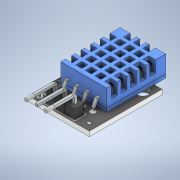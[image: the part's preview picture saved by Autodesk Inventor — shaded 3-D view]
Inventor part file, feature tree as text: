
AUTODESK INVENTOR PART (.ipt)
format: ipt  version: 2021 (Build 250183000, 183)  size: 781,824 bytes
history: native  units: mm
features: projected_geometry x5, boolean_combine x1, extrude x1, sketch x1
ambient origin geometry x8: Origin, YZ Plane, XZ Plane, XY Plane, X Axis, Y Axis, Z Axis, Center Point
bodies: Solid1 (feature_tree), Solid2 (feature_tree), Solid3 (feature_tree), Solid4 (feature_tree), Solid5 (feature_tree), Solid6 (feature_tree), Solid7 (feature_tree), Solid8 (feature_tree), Body1 (feature_tree), Body2 (feature_tree), Body3 (feature_tree), Body4 (feature_tree), Body5 (feature_tree), Body6 (feature_tree), Body7 (feature_tree), Body8 (feature_tree)
feature tree (8):
  boolean_combine  "Combine1"
  extrude  "Extrusion1"  [1 undecoded]
  sketch  "Sketch1"  dims[d0=2.0mm d1=0.0mm]
  projected_geometry  "Projected Loop1"
  projected_geometry  "Projected Loop2"
  projected_geometry  "Projected Loop3"
  projected_geometry  "Projected Loop4"
  projected_geometry  "Projected Loop5"
note: 1 required parameter value undecoded (feature->parameter linkage not recoverable at this tier; creation-order binding heuristic only, values carry confidence <= 0.55)
